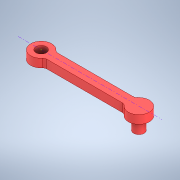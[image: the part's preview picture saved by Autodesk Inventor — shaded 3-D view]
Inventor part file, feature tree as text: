
AUTODESK INVENTOR PART (.ipt)
format: ipt  version: 2022 (Build 260153000, 153)  size: 113,152 bytes
history: imported  units: in
note: dims shown in document units (in); Inventor stores cm internally (conversion verified against a paired STEP export)
features: sketch x1, imported_body x1
ambient origin geometry x8: Origin, YZ Plane, XZ Plane, XY Plane, X Axis, Y Axis, Z Axis, Center Point
bodies: Solid1 (imported_parasolid), Body1 (imported_parasolid)
feature tree (2):
  sketch  "Sketch1"
  imported_body  NMx_Import_Brep_tag  [imported B-rep: ~13 faces, bbox_mm=[147.5, 30.0, 19.58831]]
